# Revit family: heroal S 77 Sliding Door - Connection Profile
name_source: partatom
category: Türen
revit_build: Autodesk Revit 2017 (Build: 20160225_1515(x64)
units: mm (PartAtom-declared; Revit-internal decimal feet)

## family parameters
Basisbauteil = Wand
Beim Laden mit Abzugskörper schneiden = Nein
Gemeinsam genutzt = Nein
Immer vertikal = Ja
OmniClass-Nummer = 23.30.10.00
OmniClass-Titel = Doors
Raumberechnungspunkt = Ja

## types (1)
- 46x2200
    Air Permeability DIN EN 12207 = 4
    Analytische Konstruktion = <None>
    Baugruppenkennzeichen = B2030110
    Beschreibung = heroal S 77 Sliding Systems
    Breite = 46 mm
    Burglary Resistance DIN V ENV 1627 = up to RC 2
    Heat Insulation [Uf in W/m2K] DIN EN ISO 10077 = > 2,9 W/m²K
    Heat Insulation [Uf in W/m2K]/Standard Profile View DIN EN ISO 10077 = > 2,9 W/m²K
    Heat Insulation [Uw in W/m2K] DIN EN ISO 10077-1 = > 1,1 W/m²K
    Hersteller = heroal
    Höhe = 2200 mm
    Max. Casement Leaf Height = 3000mm
    Max. Casement Weight = 150 - 400kg
    Max. Thickness Of Glass/Infill Panel = 52mm
    Modell = heroal S 77
    Profile Installation Depth - Casement Profiles = 77mm
    Profile Installation Depth - Cross Bar Profiles = 72mm
    Profile Installation Depth - Frame Profiles = 178/279mm
    Profile View Width - Casement Profiles = 94 - 104mm
    Profile View Width - Cross Bar Profiles = 74 - 104mm
    Profile View Width - Frame Profiles = 40 - 63mm
    Reveal Top = 20 mm  [stored 0.0656168 ft]
    Rohbaubreite = 46 mm
    Rohbauhöhe = 2200 mm
    Soundproofing Class DIN EN ISO 717-1 = 1-3
    Tightness Against Driving Rain DIN EN 12208 = 9A
    URL = http://www.heroal.com
    Wandabschluss = Nach Basisbauteil
    Wind Load Resistance DIN EN 12210 = C3/B3

note: [stored X ft] marks values corroborated as IEEE doubles in the binary element streams (Revit-internal decimal feet)

## geometry (parser evidence)
native form markers: Blend x2, Sweep x4
no freeform markers — native parametric forms only
